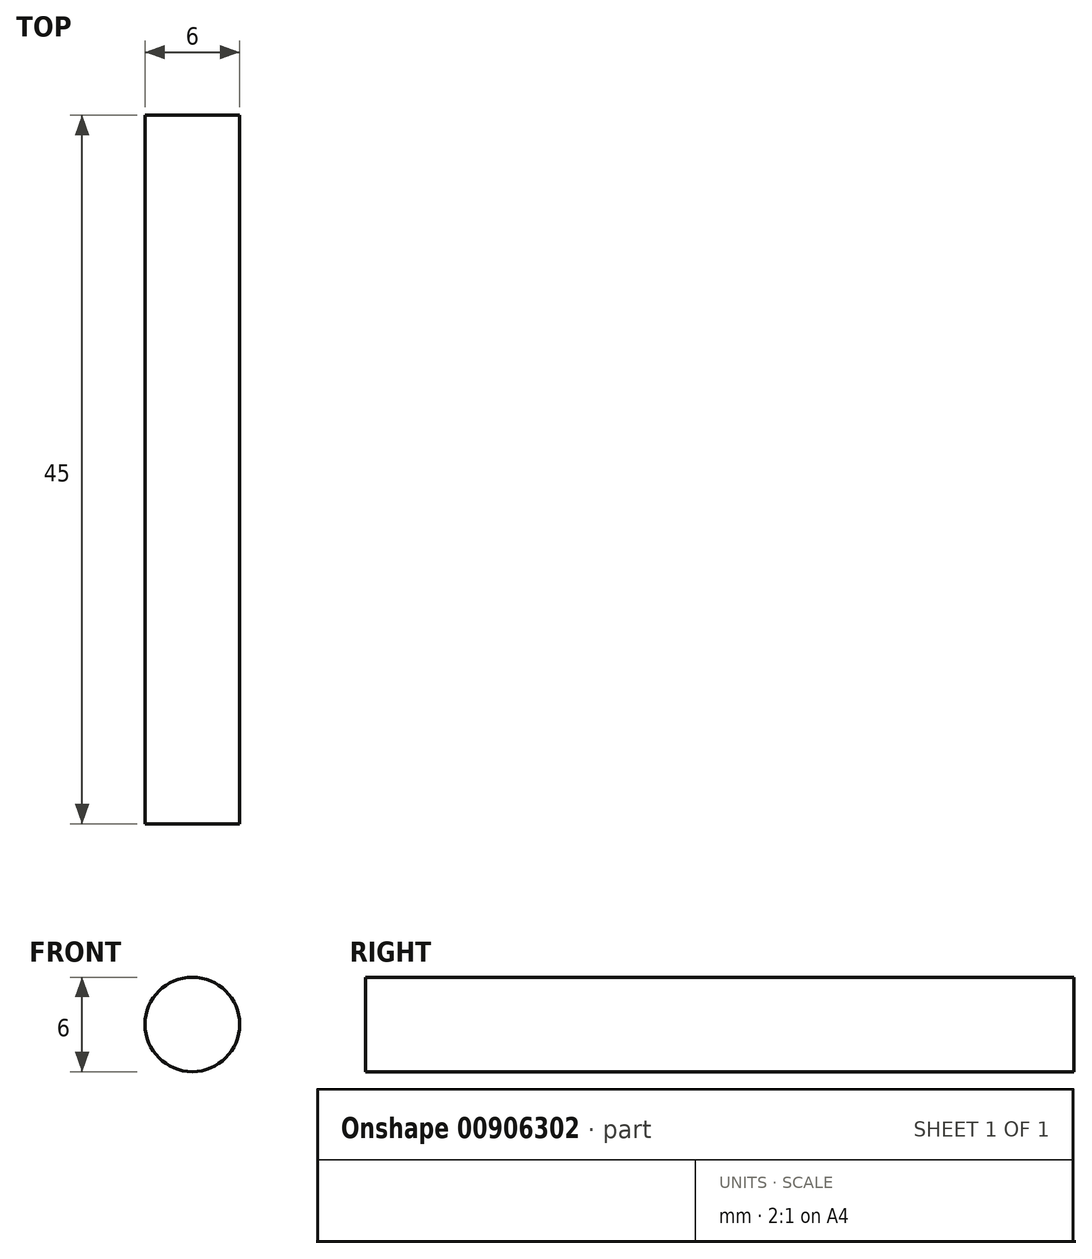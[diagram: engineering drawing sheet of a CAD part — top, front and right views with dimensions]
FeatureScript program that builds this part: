
annotation { "Feature Type Name" : "Feature", "Feature Type Description" : "" }
export const myFeature = defineFeature(function(context is Context, id is Id, definition is map)
    precondition{}
    {
        {
            var Q0;
            Q0=qCreatedBy(makeId("Front.planeOp"),FACE);
            var sketch = newSketch(context, id + "F0", { "sketchPlane" : qUnion([Q0])});
            skCircle(sketch, "E0", {"center": v(0, 0) * mm, "radius": 3 * mm});
            skSolve(sketch);
        }
        {
            var Q0;
            Q0=qCreatedBy(makeId("Right.planeOp"),FACE);
            var sketch = newSketch(context, id + "F1", { "sketchPlane" : qUnion([Q0])});
            skLineSegment(sketch, "E1", {"start": v(0, 0) * mm, "end": v(-45, 0) * mm});
            skSolve(sketch);
        }
        {
            var Q0;
            Q0=makeQuery(id+"F0.imprint","IMPRINT",FACE,{"disambiguationData":[TD([[makeQuery(id+"F0.imprint","IMPRINT",EDGE,{"derivedFrom":sQuery(id+"F0.wireOp",EDGE,"E0")}),1.0]])]});
            var Q1;
            Q1=sQuery(id+"F1.wireOp",EDGE,"E1");
            sweep(context, id + "F2", {"profiles" : qUnion([Q0]), "path" : qUnion([Q1])});
        }
    });
